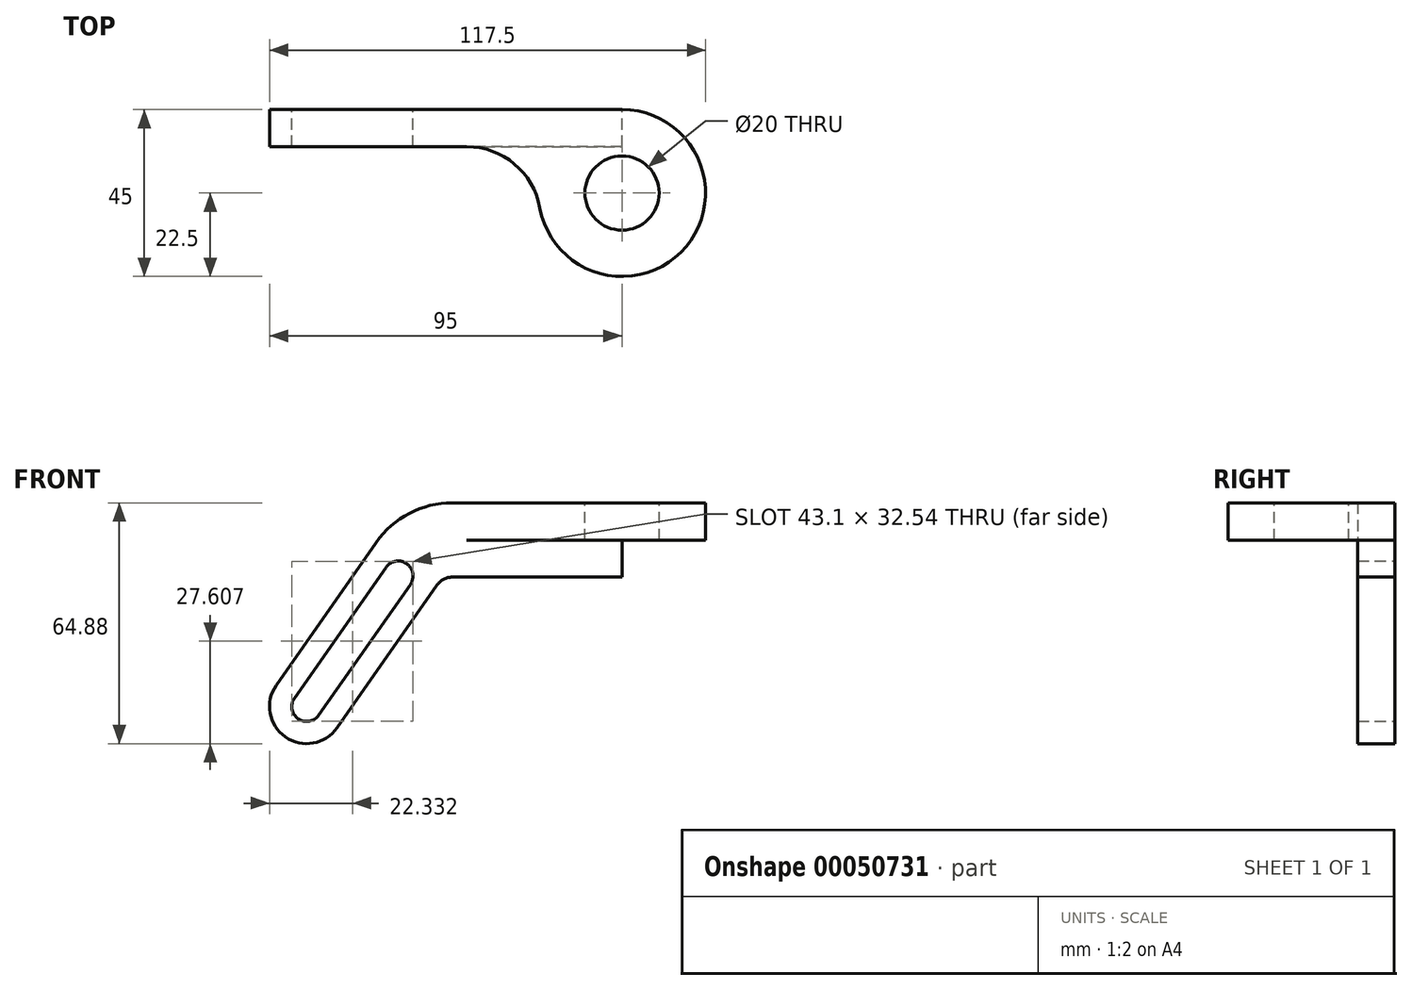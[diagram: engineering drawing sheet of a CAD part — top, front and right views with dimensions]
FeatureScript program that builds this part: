
annotation { "Feature Type Name" : "Feature", "Feature Type Description" : "" }
export const myFeature = defineFeature(function(context is Context, id is Id, definition is map)
    precondition{}
    {
        {
            var Q0;
            Q0=qCreatedBy(makeId("Top.planeOp"),FACE);
            var sketch = newSketch(context, id + "F0", { "sketchPlane" : qUnion([Q0])});
            skCircle(sketch, "E0", {"center": v(0, 0) * mm, "radius": 10 * mm});
            skCircle(sketch, "E1", {"center": v(0, 0) * mm, "radius": 22.5 * mm});
            skSolve(sketch);
        }
        {
            var Q0;
            Q0=makeQuery(id+"F0.imprint","IMPRINT",FACE,{"disambiguationData":[TD([[makeQuery(id+"F0.imprint","IMPRINT",EDGE,{"derivedFrom":sQuery(id+"F0.wireOp",EDGE,"E0")}),-1.0]])]});
            extrude(context, id + "F1", {"entities" : qUnion([Q0]), "oppositeDirection" : true, "depth" : 10 * mm});
        }
        {
            var Q0;
            Q0=qCreatedBy(makeId("Front.planeOp"),FACE);
            cPlane(context, id + "F2", {"entities" : qUnion([Q0]), "cplaneType" : CPlaneType.OFFSET, "offset" : 22.5 * mm, "oppositeDirection" : true, "width" : 150 * mm, "height" : 150 * mm});
        }
        {
            var Q0;
            Q0=qCreatedBy(id+"F2.planeOp",FACE);
            var sketch = newSketch(context, id + "F3", { "sketchPlane" : qUnion([Q0])});
            skLineSegment(sketch, "E2", {"start": v(0, 0) * mm, "end": v(-58.78, 0) * mm});
            skLineSegment(sketch, "E3", {"start": v(-58.78, 0) * mm, "end": v(-93.2, -49.15) * mm});
            skLineSegment(sketch, "E4.0", {"start": v(-48.37, -20) * mm, "end": v(-76.8, -60.62) * mm});
            skLineSegment(sketch, "E5.0", {"start": v(0, -20) * mm, "end": v(-48.37, -20) * mm});
            skLineSegment(sketch, "E6", {"start": v(-90.74, -63.08) * mm, "end": v(-90.74, -63.08) * mm});
            skLineSegment(sketch, "E7", {"start": v(0, 0) * mm, "end": v(0, -20) * mm});
            skPoint(sketch, "E8.visualSharp", {"position": v(-98.93, -57.34) * mm});
            skArc(sketch, "E8.filletArc", {"start": v(-93.2, -49.15) * mm, "mid": v(-94.85, -56.62) * mm, "end": v(-90.74, -63.08) * mm});
            skPoint(sketch, "E9.visualSharp", {"position": v(-82.54, -68.81) * mm});
            skArc(sketch, "E9.filletArc", {"start": v(-90.74, -63.08) * mm, "mid": v(-83.26, -64.73) * mm, "end": v(-76.8, -60.62) * mm});
            skLineSegment(sketch, "E10", {"start": v(-85, -54.88) * mm, "end": v(-60.34, -19.66) * mm, "construction": true});
            skArc(sketch, "E11.0.startCap", {"start": v(-81.72, -57.18) * mm, "mid": v(-87.3, -58.16) * mm, "end": v(-88.28, -52.6) * mm});
            skArc(sketch, "E11.0.endCap", {"start": v(-63.61, -17.37) * mm, "mid": v(-58.04, -16.38) * mm, "end": v(-57.06, -21.96) * mm});
            skLineSegment(sketch, "E11.0.left", {"start": v(-88.28, -52.6) * mm, "end": v(-63.61, -17.37) * mm});
            skLineSegment(sketch, "E11.0.right", {"start": v(-81.72, -57.18) * mm, "end": v(-57.06, -21.96) * mm});
            skSolve(sketch);
        }
        {
            var Q0;
            Q0=makeQuery(id+"F3.imprint","IMPRINT",FACE,{"disambiguationData":[TD([[makeQuery(id+"F3.imprint","IMPRINT",EDGE,{"derivedFrom":sQuery(id+"F3.wireOp",EDGE,"E2")}),1.0]])]});
            extrude(context, id + "F4", {"entities" : qUnion([Q0]), "operationType" : NewBodyOperationType.ADD, "depth" : 10 * mm});
        }
        {
            var Q0;
            Q0=makeQuery(id+"F4.opExtrude","SWEPT_EDGE",EDGE,{"disambiguationData":[OSD([sQuery(id+"F3.wireOp",EDGE,"E2"),sQuery(id+"F3.wireOp",EDGE,"E3")])]});
            fillet(context, id + "F5", {"entities" : qUnion([Q0]), "radius" : 25 * mm, "tangentPropagation" : true, "allowEdgeOverflow" : false});
        }
        {
            var Q0;
            Q0=makeQuery(id+"F4.opExtrude","SWEPT_EDGE",EDGE,{"disambiguationData":[OSD([sQuery(id+"F3.wireOp",EDGE,"E4.0"),sQuery(id+"F3.wireOp",EDGE,"E5.0")])]});
            fillet(context, id + "F6", {"entities" : qUnion([Q0]), "radius" : 5 * mm, "tangentPropagation" : true, "allowEdgeOverflow" : false});
        }
        {
            var Q0;
            Q0=makeQuery(id+"F4.boolean.opBoolean","INTERSECT",EDGE,{"derivedFrom":[makeQuery(id+"F1.opExtrude","SWEPT_FACE",FACE,{"disambiguationData":[OSD([sQuery(id+"F0.wireOp",EDGE,"E1")])]}),makeQuery(id+"F4.opExtrude","CAP_FACE",FACE,{"disambiguationData":[OSD([sQuery(id+"F3.wireOp",EDGE,"E2"),sQuery(id+"F3.wireOp",EDGE,"E3"),sQuery(id+"F3.wireOp",EDGE,"E4.0"),sQuery(id+"F3.wireOp",EDGE,"E5.0"),sQuery(id+"F3.wireOp",EDGE,"E7"),sQuery(id+"F3.wireOp",EDGE,"E8.filletArc"),sQuery(id+"F3.wireOp",EDGE,"E9.filletArc"),sQuery(id+"F3.wireOp",EDGE,"E11.0.startCap"),sQuery(id+"F3.wireOp",EDGE,"E11.0.endCap"),sQuery(id+"F3.wireOp",EDGE,"E11.0.left"),sQuery(id+"F3.wireOp",EDGE,"E11.0.right")])],"isStart":false})]});
            fillet(context, id + "F7", {"entities" : qUnion([Q0]), "radius" : 20 * mm, "tangentPropagation" : true, "allowEdgeOverflow" : false});
        }
    });
